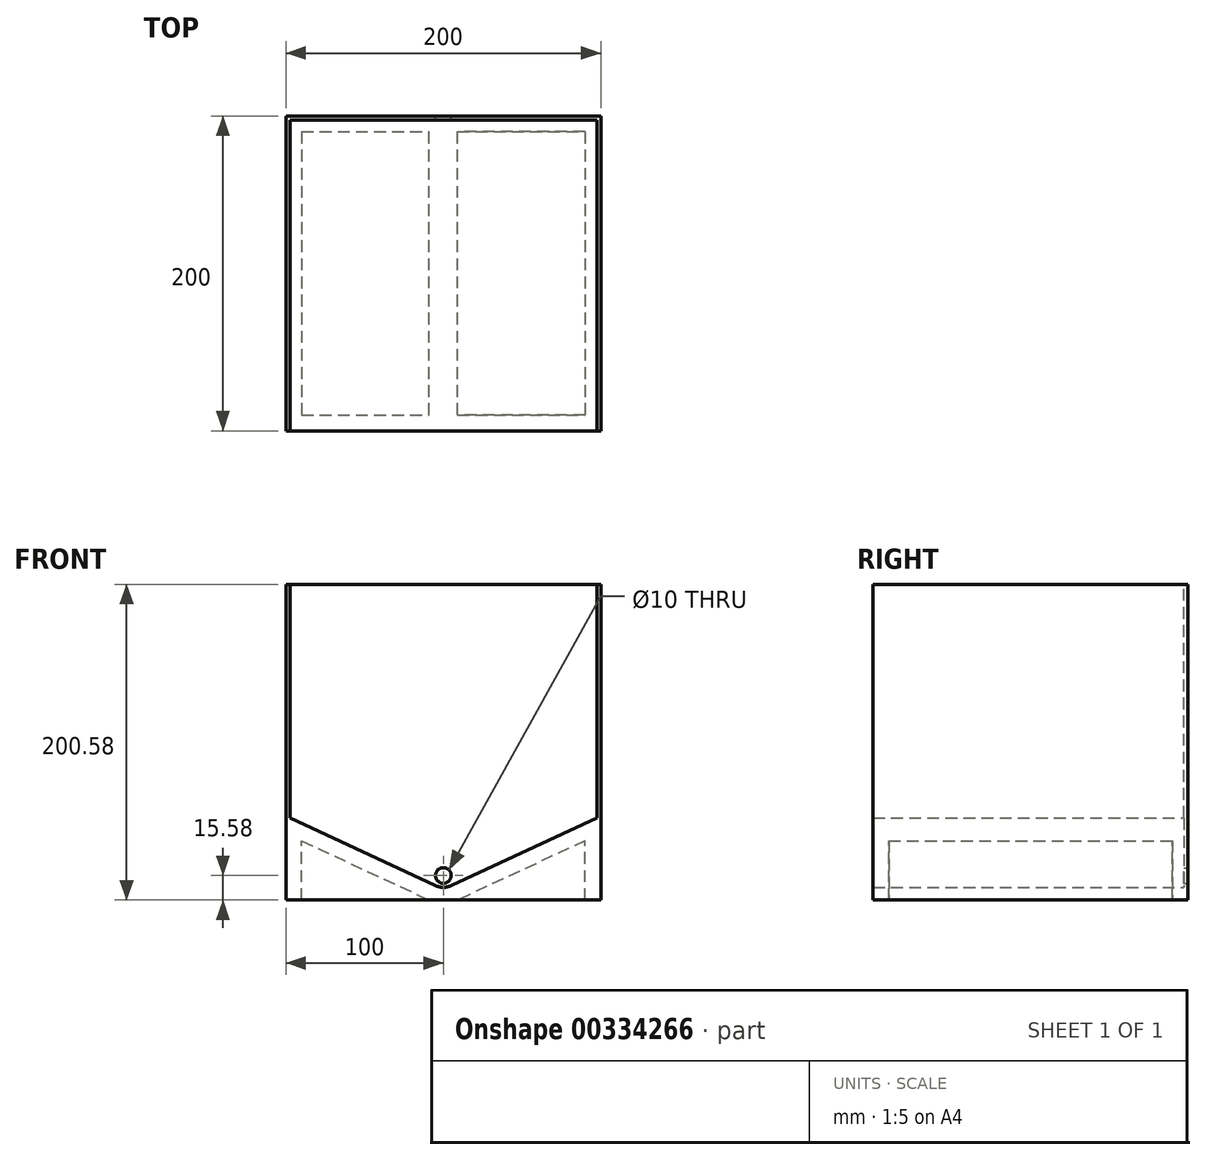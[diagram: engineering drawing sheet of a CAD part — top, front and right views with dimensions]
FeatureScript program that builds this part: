
annotation { "Feature Type Name" : "Feature", "Feature Type Description" : "" }
export const myFeature = defineFeature(function(context is Context, id is Id, definition is map)
    precondition{}
    {
        {
            var Q0;
            Q0=qCreatedBy(makeId("Front.planeOp"),FACE);
            var sketch = newSketch(context, id + "F0", { "sketchPlane" : qUnion([Q0])});
            skLineSegment(sketch, "E0.top", {"start": v(0, 150) * mm, "end": v(200, 150) * mm});
            skLineSegment(sketch, "E0.left", {"start": v(0, 0) * mm, "end": v(0, 150) * mm});
            skLineSegment(sketch, "E0.right", {"start": v(200, 0) * mm, "end": v(200, 150) * mm});
            skCircle(sketch, "E1", {"center": v(100, -30) * mm, "radius": 15 * mm});
            skLineSegment(sketch, "E2", {"start": v(0, 0) * mm, "end": v(93.67, -43.6) * mm});
            skLineSegment(sketch, "E3", {"start": v(200, 0) * mm, "end": v(106.33, -43.6) * mm});
            skSolve(sketch);
        }
        {
            var Q0;
            Q0=makeQuery(id+"F0.imprint","IMPRINT",FACE,{"disambiguationData":[TD([[makeQuery(id+"F0.imprint","IMPRINT",EDGE,{"derivedFrom":sQuery(id+"F0.wireOp",EDGE,"E0.top")}),-1.0]])]});
            var Q1;
            {var subQ0=sQuery(id+"F0.wireOp",EDGE,"E1");var subQ1=makeQuery(id+"F0.imprint","INTERSECT",VERTEX,{"derivedFrom":[subQ0,sQuery(id+"F0.wireOp",EDGE,"E2")]});Q1=makeQuery(id+"F0.imprint","IMPRINT",FACE,{"disambiguationData":[TD([[makeQuery(id+"F0.imprint","IMPRINT",EDGE,{"disambiguationData":[TD([[subQ1,-1.0]])],"derivedFrom":subQ0}),1.0]])]});}
            extrude(context, id + "F1", {"entities" : qUnion([Q0, Q1]), "endBound" : BoundingType.SYMMETRIC, "depth" : 200 * mm});
        }
        {
            var Q0;
            Q0=makeQuery(id+"F1.opExtrude","CAP_FACE",FACE,{"disambiguationData":[OSD([sQuery(id+"F0.wireOp",EDGE,"E0.top"),sQuery(id+"F0.wireOp",EDGE,"E0.left"),sQuery(id+"F0.wireOp",EDGE,"E0.right"),sQuery(id+"F0.wireOp",EDGE,"E1"),sQuery(id+"F0.wireOp",EDGE,"E2"),sQuery(id+"F0.wireOp",EDGE,"E3")])],"isStart":false});
            var Q1;
            Q1=makeQuery(id+"F1.opExtrude","SWEPT_FACE",FACE,{"disambiguationData":[OSD([sQuery(id+"F0.wireOp",EDGE,"E0.top")])]});
            shell(context, id + "F2", {"entities" : qUnion([Q0, Q1]), "thickness" : 2.5 * mm});
        }
        {
            var Q0;
            Q0=makeQuery(id+"F1.opExtrude","CAP_FACE",FACE,{"disambiguationData":[OSD([sQuery(id+"F0.wireOp",EDGE,"E0.top"),sQuery(id+"F0.wireOp",EDGE,"E0.left"),sQuery(id+"F0.wireOp",EDGE,"E0.right"),sQuery(id+"F0.wireOp",EDGE,"E1"),sQuery(id+"F0.wireOp",EDGE,"E2"),sQuery(id+"F0.wireOp",EDGE,"E3")])],"isStart":true});
            var sketch = newSketch(context, id + "F3", { "sketchPlane" : qUnion([Q0])});
            skCircle(sketch, "E4", {"center": v(-100, -35) * mm, "radius": 5 * mm});
            skSolve(sketch);
        }
        {
            var Q0;
            Q0 = qSketchRegion(id + "F3", true);
            extrude(context, id + "F4", {"entities" : qUnion([Q0]), "operationType" : NewBodyOperationType.REMOVE, "endBound" : BoundingType.THROUGH_ALL, "oppositeDirection" : true, "depth" : 25 * mm});
        }
        {
            var Q0;
            Q0=makeQuery(id+"F1.opExtrude","CAP_FACE",FACE,{"disambiguationData":[OSD([sQuery(id+"F0.wireOp",EDGE,"E0.top"),sQuery(id+"F0.wireOp",EDGE,"E0.left"),sQuery(id+"F0.wireOp",EDGE,"E0.right"),sQuery(id+"F0.wireOp",EDGE,"E1"),sQuery(id+"F0.wireOp",EDGE,"E2"),sQuery(id+"F0.wireOp",EDGE,"E3")])],"isStart":false});
            var sketch = newSketch(context, id + "F5", { "sketchPlane" : qUnion([Q0])});
            skLineSegment(sketch, "E5", {"start": v(0, 0) * mm, "end": v(0, -50.58) * mm});
            skLineSegment(sketch, "E6", {"start": v(0, -50.58) * mm, "end": v(200, -50.58) * mm});
            skLineSegment(sketch, "E7", {"start": v(200, -50.58) * mm, "end": v(200, 0) * mm});
            skLineSegment(sketch, "E8", {"start": v(200, 0) * mm, "end": v(106.33, -43.6) * mm});
            skLineSegment(sketch, "E9", {"start": v(106.33, -43.6) * mm, "end": v(100, -45) * mm});
            skPoint(sketch, "E9.endSnap0", {"position": v(100, -50.58) * mm});
            skLineSegment(sketch, "E10", {"start": v(100, -45) * mm, "end": v(93.67, -43.6) * mm});
            skLineSegment(sketch, "E11", {"start": v(93.67, -43.6) * mm, "end": v(0, 0) * mm});
            skSolve(sketch);
        }
        {
            var Q0;
            Q0=makeQuery(id+"F5.imprint","IMPRINT",FACE,{"disambiguationData":[TD([[makeQuery(id+"F5.imprint","IMPRINT",EDGE,{"derivedFrom":sQuery(id+"F5.wireOp",EDGE,"E5")}),1.0]])]});
            extrude(context, id + "F6", {"entities" : qUnion([Q0]), "operationType" : NewBodyOperationType.ADD, "oppositeDirection" : true, "depth" : 200 * mm});
        }
        {
            var Q0;
            Q0=makeQuery(id+"F6.opExtrude","SWEPT_FACE",FACE,{"disambiguationData":[OSD([sQuery(id+"F5.wireOp",EDGE,"E6")])]});
            shell(context, id + "F7", {"entities" : qUnion([Q0]), "thickness" : 10 * mm});
        }
    });
